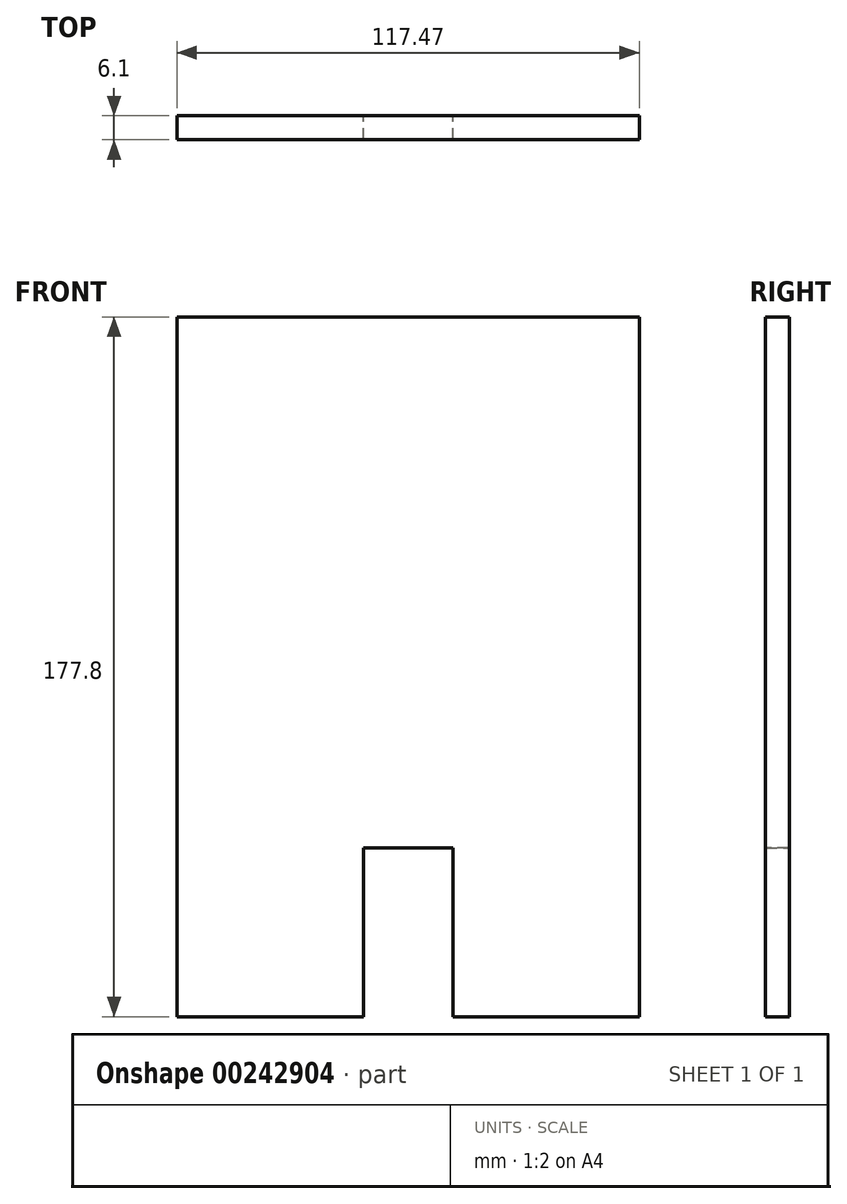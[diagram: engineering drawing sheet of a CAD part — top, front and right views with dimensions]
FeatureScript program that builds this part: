
annotation { "Feature Type Name" : "Feature", "Feature Type Description" : "" }
export const myFeature = defineFeature(function(context is Context, id is Id, definition is map)
    precondition{}
    {
        {
            var Q0;
            Q0=qCreatedBy(makeId("Front.planeOp"),FACE);
            var sketch = newSketch(context, id + "F0", { "sketchPlane" : qUnion([Q0])});
            skLineSegment(sketch, "E0", {"start": v(0, 0) * mm, "end": v(0, 177.8) * mm});
            skLineSegment(sketch, "E1", {"start": v(0, 177.8) * mm, "end": v(117.47, 177.8) * mm});
            skLineSegment(sketch, "E2", {"start": v(117.47, 177.8) * mm, "end": v(117.47, 0) * mm});
            skLineSegment(sketch, "E3", {"start": v(47.62, 0) * mm, "end": v(0, 0) * mm});
            skLineSegment(sketch, "E4", {"start": v(117.47, 0) * mm, "end": v(69.85, 0) * mm});
            skLineSegment(sketch, "E5", {"start": v(69.85, 0) * mm, "end": v(69.85, 42.86) * mm});
            skLineSegment(sketch, "E6", {"start": v(69.85, 42.86) * mm, "end": v(47.62, 42.86) * mm});
            skLineSegment(sketch, "E7", {"start": v(47.62, 42.86) * mm, "end": v(47.62, 0) * mm});
            skSolve(sketch);
        }
        {
            var Q0;
            Q0=makeQuery(id+"F0.imprint","IMPRINT",FACE,{"disambiguationData":[TD([[makeQuery(id+"F0.imprint","IMPRINT",EDGE,{"derivedFrom":sQuery(id+"F0.wireOp",EDGE,"E0")}),-1.0]])]});
            extrude(context, id + "F1", {"entities" : qUnion([Q0]), "depth" : 6.35 * mm});
        }
        {
            var Q0;
            Q0=makeQuery(id+"F1.opExtrude","SWEPT_FACE",FACE,{"disambiguationData":[OSD([sQuery(id+"F0.wireOp",EDGE,"E3")])]});
            var sketch = newSketch(context, id + "F2", { "sketchPlane" : qUnion([Q0])});
            skLineSegment(sketch, "E8", {"start": v(47.62, 0) * mm, "end": v(47.62, 6.35) * mm});
            skLineSegment(sketch, "E9", {"start": v(47.62, 6.35) * mm, "end": v(47.37, 6.35) * mm});
            skLineSegment(sketch, "E10", {"start": v(47.37, 6.35) * mm, "end": v(47.37, 0) * mm});
            skLineSegment(sketch, "E11", {"start": v(47.37, 0) * mm, "end": v(47.62, 0) * mm});
            skSolve(sketch);
        }
        {
            var Q0;
            Q0=makeQuery(id+"F2.imprint","IMPRINT",FACE,{"disambiguationData":[TD([[makeQuery(id+"F2.imprint","IMPRINT",EDGE,{"derivedFrom":sQuery(id+"F2.wireOp",EDGE,"E8")}),-1.0]])]});
            extrude(context, id + "F3", {"entities" : qUnion([Q0]), "operationType" : NewBodyOperationType.REMOVE, "oppositeDirection" : true, "depth" : 42.86 * mm});
        }
        {
            var Q0;
            Q0=makeQuery(id+"F1.opExtrude","SWEPT_FACE",FACE,{"disambiguationData":[OSD([sQuery(id+"F0.wireOp",EDGE,"E4")])]});
            var sketch = newSketch(context, id + "F4", { "sketchPlane" : qUnion([Q0])});
            skLineSegment(sketch, "E12", {"start": v(69.85, 0) * mm, "end": v(69.85, 6.35) * mm});
            skLineSegment(sketch, "E13", {"start": v(69.85, 6.35) * mm, "end": v(70.1, 6.35) * mm});
            skLineSegment(sketch, "E14", {"start": v(70.1, 6.35) * mm, "end": v(70.1, 0) * mm});
            skLineSegment(sketch, "E15", {"start": v(70.1, 0) * mm, "end": v(69.85, 0) * mm});
            skSolve(sketch);
        }
        {
            var Q0;
            Q0=makeQuery(id+"F4.imprint","IMPRINT",FACE,{"disambiguationData":[TD([[makeQuery(id+"F4.imprint","IMPRINT",EDGE,{"derivedFrom":sQuery(id+"F4.wireOp",EDGE,"E12")}),1.0]])]});
            extrude(context, id + "F5", {"entities" : qUnion([Q0]), "operationType" : NewBodyOperationType.REMOVE, "oppositeDirection" : true, "depth" : 42.86 * mm});
        }
        {
            var Q0;
            Q0=makeQuery(id+"F1.opExtrude","CAP_FACE",FACE,{"disambiguationData":[OSD([sQuery(id+"F0.wireOp",EDGE,"E0"),sQuery(id+"F0.wireOp",EDGE,"E1"),sQuery(id+"F0.wireOp",EDGE,"E2"),sQuery(id+"F0.wireOp",EDGE,"E3"),sQuery(id+"F0.wireOp",EDGE,"E4"),sQuery(id+"F0.wireOp",EDGE,"E5"),sQuery(id+"F0.wireOp",EDGE,"E6"),sQuery(id+"F0.wireOp",EDGE,"E7")])],"isStart":false});
            var sketch = newSketch(context, id + "F6", { "sketchPlane" : qUnion([Q0])});
            skLineSegment(sketch, "E16", {"start": v(0, 0) * mm, "end": v(0, 177.8) * mm});
            skLineSegment(sketch, "E17", {"start": v(0, 177.8) * mm, "end": v(117.47, 177.8) * mm});
            skLineSegment(sketch, "E18", {"start": v(117.47, 177.8) * mm, "end": v(117.47, 0) * mm});
            skLineSegment(sketch, "E19", {"start": v(117.47, 0) * mm, "end": v(70.1, 0) * mm});
            skLineSegment(sketch, "E20", {"start": v(70.1, 0) * mm, "end": v(70.1, 42.86) * mm});
            skLineSegment(sketch, "E21", {"start": v(70.1, 42.86) * mm, "end": v(47.37, 42.86) * mm});
            skLineSegment(sketch, "E22", {"start": v(47.37, 42.86) * mm, "end": v(47.37, 0) * mm});
            skLineSegment(sketch, "E23", {"start": v(47.37, 0) * mm, "end": v(0, 0) * mm});
            skSolve(sketch);
        }
        {
            var Q0;
            Q0=makeQuery(id+"F6.imprint","IMPRINT",FACE,{"disambiguationData":[TD([[makeQuery(id+"F6.imprint","IMPRINT",EDGE,{"derivedFrom":sQuery(id+"F6.wireOp",EDGE,"E16")}),-1.0]])]});
            extrude(context, id + "F7", {"entities" : qUnion([Q0]), "operationType" : NewBodyOperationType.REMOVE, "oppositeDirection" : true, "depth" : 0.25 * mm});
        }
    });
